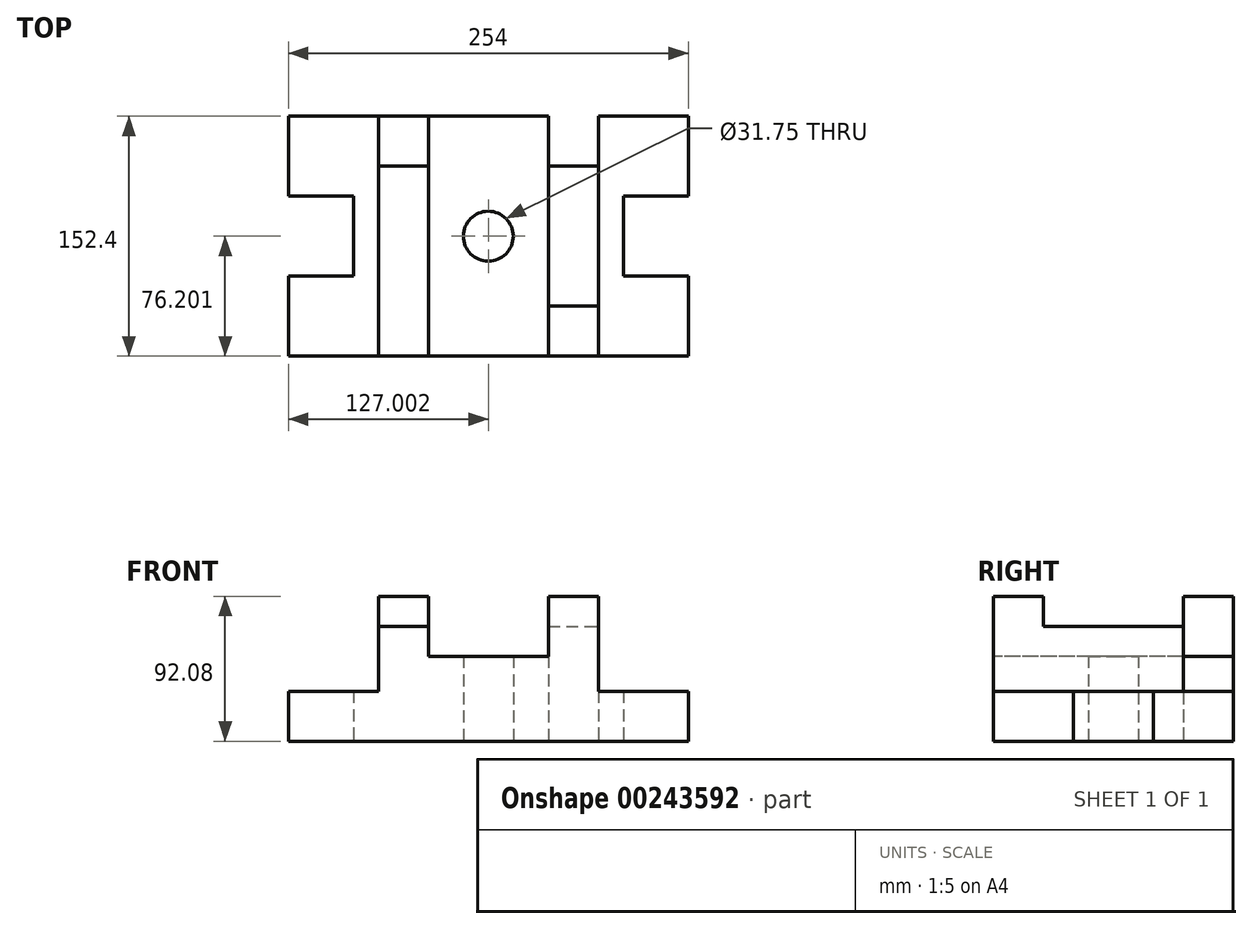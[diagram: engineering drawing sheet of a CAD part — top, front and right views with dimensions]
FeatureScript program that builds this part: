
annotation { "Feature Type Name" : "Feature", "Feature Type Description" : "" }
export const myFeature = defineFeature(function(context is Context, id is Id, definition is map)
    precondition{}
    {
        {
            var Q0;
            Q0=qCreatedBy(makeId("Top.planeOp"),FACE);
            var sketch = newSketch(context, id + "F0", { "sketchPlane" : qUnion([Q0])});
            skLineSegment(sketch, "E0", {"start": v(-123.17, -47.23) * mm, "end": v(130.83, -47.23) * mm});
            skLineSegment(sketch, "E1", {"start": v(-123.17, -47.23) * mm, "end": v(-123.17, 3.57) * mm});
            skLineSegment(sketch, "E2", {"start": v(-123.17, 3.57) * mm, "end": v(-81.9, 3.57) * mm});
            skLineSegment(sketch, "E3", {"start": v(-81.9, 3.57) * mm, "end": v(-81.9, 54.37) * mm});
            skLineSegment(sketch, "E4", {"start": v(-81.9, 54.37) * mm, "end": v(-123.17, 54.37) * mm});
            skLineSegment(sketch, "E5", {"start": v(-123.17, 54.37) * mm, "end": v(-123.17, 105.17) * mm});
            skLineSegment(sketch, "E6", {"start": v(-123.17, 105.17) * mm, "end": v(130.83, 105.17) * mm});
            skLineSegment(sketch, "E7.MirrorCS", {"start": v(130.83, 54.37) * mm, "end": v(130.83, 105.17) * mm});
            skLineSegment(sketch, "E8.MirrorCS", {"start": v(89.56, 54.37) * mm, "end": v(130.83, 54.37) * mm});
            skLineSegment(sketch, "E9.MirrorCS", {"start": v(89.56, 3.57) * mm, "end": v(89.56, 54.37) * mm});
            skLineSegment(sketch, "E10.MirrorCS", {"start": v(130.83, 3.57) * mm, "end": v(89.56, 3.57) * mm});
            skLineSegment(sketch, "E11.MirrorCS", {"start": v(130.83, -47.23) * mm, "end": v(130.83, 3.57) * mm});
            skLineSegment(sketch, "E12", {"start": v(130.83, 105.17) * mm, "end": v(73.68, 105.17) * mm});
            skLineSegment(sketch, "E13", {"start": v(73.68, 105.17) * mm, "end": v(41.93, 105.17) * mm});
            skLineSegment(sketch, "E14", {"start": v(73.68, 105.17) * mm, "end": v(73.68, -47.23) * mm});
            skLineSegment(sketch, "E15", {"start": v(41.93, 105.17) * mm, "end": v(41.93, -47.23) * mm});
            skLineSegment(sketch, "E16.MirrorCS", {"start": v(-34.27, 105.17) * mm, "end": v(-34.27, -47.23) * mm});
            skLineSegment(sketch, "E17", {"start": v(-66.02, 105.17) * mm, "end": v(-66.02, 73.42) * mm});
            skLineSegment(sketch, "E18", {"start": v(-66.02, 73.42) * mm, "end": v(-66.02, -47.23) * mm});
            skLineSegment(sketch, "E19", {"start": v(-66.02, -47.23) * mm, "end": v(-66.02, -15.48) * mm});
            skLineSegment(sketch, "E20", {"start": v(-66.02, 105.17) * mm, "end": v(-34.27, 105.17) * mm});
            skLineSegment(sketch, "E21", {"start": v(-66.02, 73.42) * mm, "end": v(-34.27, 73.42) * mm});
            skLineSegment(sketch, "E22", {"start": v(-66.02, -15.48) * mm, "end": v(-34.27, -15.48) * mm});
            skLineSegment(sketch, "E23", {"start": v(41.93, 73.42) * mm, "end": v(73.68, 73.42) * mm});
            skLineSegment(sketch, "E24", {"start": v(41.93, -15.48) * mm, "end": v(73.68, -15.48) * mm});
            skLineSegment(sketch, "E25", {"start": v(-81.9, 3.57) * mm, "end": v(-81.9, 28.97) * mm});
            skCircle(sketch, "E26", {"center": v(3.83, 28.97) * mm, "radius": 15.88 * mm});
            skSolve(sketch);
        }
        {
            var Q0;
            {var subQ0=sQuery(id+"F0.wireOp",EDGE,"E1");Q0=makeQuery(id+"F0.imprint","IMPRINT",FACE,{"disambiguationData":[TD([[makeQuery(id+"F0.imprint","IMPRINT",EDGE,{"derivedFrom":subQ0}),-1.0]])]});}
            var Q1;
            Q1=makeQuery(id+"F0.imprint","IMPRINT",FACE,{"disambiguationData":[TD([[makeQuery(id+"F0.imprint","IMPRINT",EDGE,{"derivedFrom":sQuery(id+"F0.wireOp",EDGE,"E7.MirrorCS")}),1.0]])]});
            extrude(context, id + "F1", {"entities" : qUnion([Q0, Q1]), "depth" : 31.75 * mm});
        }
        {
            var Q0;
            {var subQ0=sQuery(id+"F0.wireOp",EDGE,"E15");var subQ4=sQuery(id+"F0.wireOp",EDGE,"E0");var subQ5=makeQuery(id+"F0.imprint","INTERSECT",VERTEX,{"derivedFrom":[subQ4,subQ0]});Q0=makeQuery(id+"F0.imprint","IMPRINT",FACE,{"disambiguationData":[TD([[makeQuery(id+"F0.imprint","IMPRINT",EDGE,{"disambiguationData":[TD([[subQ5,1.0]])],"derivedFrom":subQ4}),1.0]])]});}
            extrude(context, id + "F2", {"entities" : qUnion([Q0]), "operationType" : NewBodyOperationType.ADD, "depth" : 53.97 * mm});
        }
        {
            var Q0;
            {var subQ3=sQuery(id+"F0.wireOp",EDGE,"E19");Q0=makeQuery(id+"F0.imprint","IMPRINT",FACE,{"disambiguationData":[TD([[makeQuery(id+"F0.imprint","IMPRINT",EDGE,{"derivedFrom":subQ3}),-1.0]])]});}
            var Q1;
            Q1=makeQuery(id+"F0.imprint","IMPRINT",FACE,{"disambiguationData":[TD([[makeQuery(id+"F0.imprint","IMPRINT",EDGE,{"derivedFrom":sQuery(id+"F0.wireOp",EDGE,"E17")}),1.0]])]});
            var Q2;
            {var subQ5=sQuery(id+"F0.wireOp",EDGE,"E24");Q2=makeQuery(id+"F0.imprint","IMPRINT",FACE,{"disambiguationData":[TD([[makeQuery(id+"F0.imprint","IMPRINT",EDGE,{"derivedFrom":subQ5}),-1.0]])]});}
            var Q3;
            {var subQ0=sQuery(id+"F0.wireOp",EDGE,"E13");Q3=makeQuery(id+"F0.imprint","IMPRINT",FACE,{"disambiguationData":[TD([[makeQuery(id+"F0.imprint","IMPRINT",EDGE,{"derivedFrom":subQ0}),1.0]])]});}
            extrude(context, id + "F3", {"entities" : qUnion([Q0, Q1, Q2, Q3]), "operationType" : NewBodyOperationType.ADD, "depth" : 92.07 * mm});
        }
        {
            var Q0;
            Q0=makeQuery(id+"F0.imprint","IMPRINT",FACE,{"disambiguationData":[TD([[makeQuery(id+"F0.imprint","IMPRINT",EDGE,{"derivedFrom":sQuery(id+"F0.wireOp",EDGE,"E18")}),1.0]])]});
            var Q1;
            {var subQ0=sQuery(id+"F0.wireOp",EDGE,"E23");Q1=makeQuery(id+"F0.imprint","IMPRINT",FACE,{"disambiguationData":[TD([[makeQuery(id+"F0.imprint","IMPRINT",EDGE,{"derivedFrom":subQ0}),-1.0]])]});}
            extrude(context, id + "F4", {"entities" : qUnion([Q0, Q1]), "operationType" : NewBodyOperationType.ADD, "depth" : 73.02 * mm});
        }
    });
